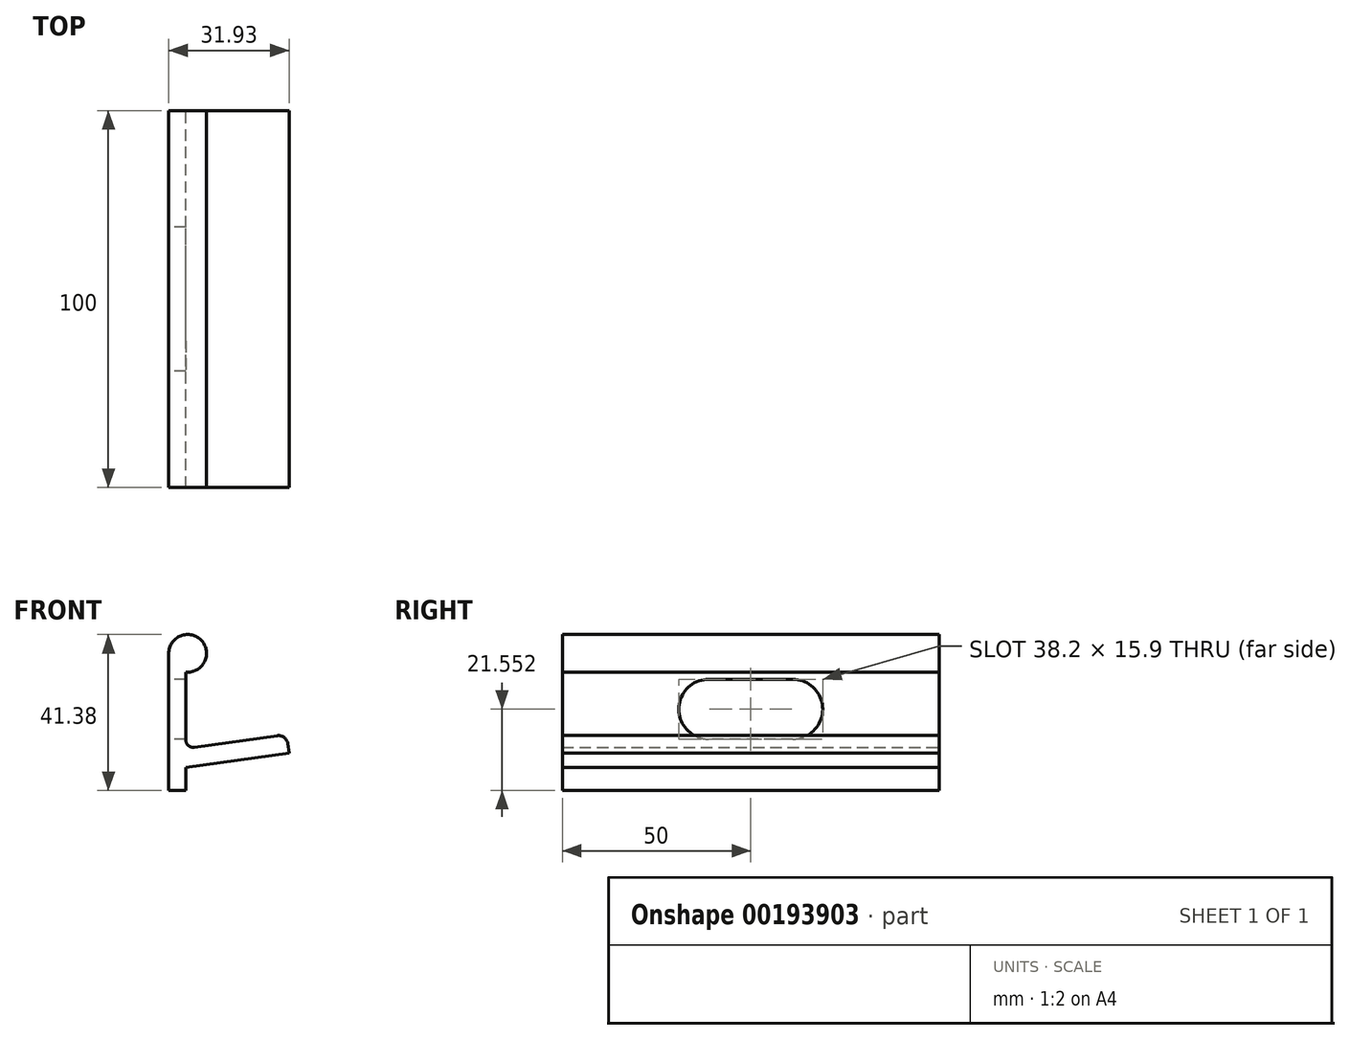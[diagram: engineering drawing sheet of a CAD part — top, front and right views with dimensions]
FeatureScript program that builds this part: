
annotation { "Feature Type Name" : "Feature", "Feature Type Description" : "" }
export const myFeature = defineFeature(function(context is Context, id is Id, definition is map)
    precondition{}
    {
        {
            var Q0;
            Q0=qCreatedBy(makeId("Front.planeOp"),FACE);
            var sketch = newSketch(context, id + "F0", { "sketchPlane" : qUnion([Q0])});
            skLineSegment(sketch, "E0", {"start": v(0, 29.9) * mm, "end": v(0, 7.11) * mm});
            skLineSegment(sketch, "E1", {"start": v(4.5, 23.01) * mm, "end": v(4.5, 7.11) * mm});
            skLineSegment(sketch, "E2", {"start": v(4.5, -0.4) * mm, "end": v(4.5, -6.49) * mm});
            skLineSegment(sketch, "E3", {"start": v(28.76, 8.06) * mm, "end": v(6.78, 4.97) * mm});
            skLineSegment(sketch, "E4", {"start": v(31.59, 5.93) * mm, "end": v(31.93, 3.46) * mm});
            skLineSegment(sketch, "E5", {"start": v(31.93, 3.46) * mm, "end": v(4.5, -0.4) * mm});
            skPoint(sketch, "E6.visualSharp", {"position": v(31.24, 8.4) * mm});
            skArc(sketch, "E6.filletArc", {"start": v(31.59, 5.93) * mm, "mid": v(30.61, 7.58) * mm, "end": v(28.76, 8.06) * mm});
            skLineSegment(sketch, "E7", {"start": v(4.5, 7.11) * mm, "end": v(0, 7.11) * mm});
            skLineSegment(sketch, "E8", {"start": v(4.5, 7.11) * mm, "end": v(4.5, 6.95) * mm});
            skPoint(sketch, "E9.visualSharp", {"position": v(4.5, 4.65) * mm});
            skArc(sketch, "E9.filletArc", {"start": v(4.5, 6.95) * mm, "mid": v(5.19, 5.44) * mm, "end": v(6.78, 4.97) * mm});
            skLineSegment(sketch, "E10", {"start": v(4.5, 23.01) * mm, "end": v(4.5, 24.92) * mm});
            skLineSegment(sketch, "E11", {"start": v(0, 29.9) * mm, "end": v(5, 29.9) * mm, "construction": true});
            skArc(sketch, "E12", {"start": v(4.5, 24.92) * mm, "mid": v(8.7, 33.25) * mm, "end": v(0, 29.9) * mm});
            skLineSegment(sketch, "E13", {"start": v(0, 7.11) * mm, "end": v(0, -6.49) * mm});
            skLineSegment(sketch, "E14", {"start": v(0, -6.49) * mm, "end": v(4.5, -6.49) * mm});
            skLineSegment(sketch, "E15", {"start": v(4.5, 23.01) * mm, "end": v(10.72, 23.01) * mm, "construction": true});
            skLineSegment(sketch, "E16", {"start": v(5, 29.9) * mm, "end": v(5, 34.9) * mm, "construction": true});
            skLineSegment(sketch, "E17", {"start": v(5, 34.9) * mm, "end": v(-15.33, 34.9) * mm, "construction": true});
            skLineSegment(sketch, "E18", {"start": v(-9.2, 4.65) * mm, "end": v(4.5, 4.65) * mm, "construction": true});
            skLineSegment(sketch, "E19", {"start": v(0, 7.11) * mm, "end": v(-9.32, 7.11) * mm, "construction": true});
            skLineSegment(sketch, "E20", {"start": v(4.5, 23.01) * mm, "end": v(0, 23.01) * mm});
            skLineSegment(sketch, "E21", {"start": v(4.5, 11.64) * mm, "end": v(4.5, 6.95) * mm});
            skLineSegment(sketch, "E22", {"start": v(6.78, 4.97) * mm, "end": v(4.5, 4.65) * mm, "construction": true});
            skLineSegment(sketch, "E23", {"start": v(4.5, 4.65) * mm, "end": v(4.5, 7.11) * mm, "construction": true});
            skLineSegment(sketch, "E24", {"start": v(-18.19, 15.06) * mm, "end": v(19.73, 15.06) * mm, "construction": true});
            skSolve(sketch);
        }
        {
            var Q0;
            Q0=makeQuery(id+"F0.imprint","IMPRINT",FACE,{"disambiguationData":[TD([[makeQuery(id+"F0.imprint","IMPRINT",EDGE,{"derivedFrom":sQuery(id+"F0.wireOp",EDGE,"E2")}),-1.0]])]});
            var Q1;
            {var subQ3=sQuery(id+"F0.wireOp",EDGE,"E1");Q1=makeQuery(id+"F0.imprint","IMPRINT",FACE,{"disambiguationData":[TD([[makeQuery(id+"F0.imprint","IMPRINT",EDGE,{"derivedFrom":subQ3}),-1.0]])]});}
            var Q2;
            Q2=makeQuery(id+"F0.imprint","IMPRINT",FACE,{"disambiguationData":[TD([[makeQuery(id+"F0.imprint","IMPRINT",EDGE,{"derivedFrom":sQuery(id+"F0.wireOp",EDGE,"E10")}),1.0]])]});
            extrude(context, id + "F1", {"entities" : qUnion([Q0, Q1, Q2]), "endBound" : BoundingType.SYMMETRIC, "depth" : 100 * mm});
        }
        {
            var Q0;
            Q0=makeQuery(id+"F1.opExtrude","SWEPT_FACE",FACE,{"disambiguationData":[OSD([sQuery(id+"F0.wireOp",EDGE,"E0"),sQuery(id+"F0.wireOp",EDGE,"E13")])]});
            var sketch = newSketch(context, id + "F2", { "sketchPlane" : qUnion([Q0])});
            skLineSegment(sketch, "E25", {"start": v(0, 15.06) * mm, "end": v(19.1, 15.06) * mm, "construction": true});
            skLineSegment(sketch, "E26.MirrorCS", {"start": v(0, 15.06) * mm, "end": v(-19.1, 15.06) * mm, "construction": true});
            skArc(sketch, "E27", {"start": v(11.15, 7.11) * mm, "mid": v(19.1, 15.06) * mm, "end": v(11.15, 23.01) * mm});
            skArc(sketch, "E28", {"start": v(-11.15, 23.01) * mm, "mid": v(-19.1, 15.06) * mm, "end": v(-11.15, 7.11) * mm});
            skLineSegment(sketch, "E29", {"start": v(-11.15, 23.01) * mm, "end": v(11.15, 23.01) * mm});
            skLineSegment(sketch, "E30", {"start": v(11.15, 7.11) * mm, "end": v(-11.15, 7.11) * mm});
            skSolve(sketch);
        }
        {
            var Q0;
            Q0=makeQuery(id+"F2.imprint","IMPRINT",FACE,{"disambiguationData":[TD([[makeQuery(id+"F2.imprint","IMPRINT",EDGE,{"derivedFrom":sQuery(id+"F2.wireOp",EDGE,"E27")}),1.0]])]});
            extrude(context, id + "F3", {"entities" : qUnion([Q0]), "operationType" : NewBodyOperationType.REMOVE, "oppositeDirection" : true, "depth" : 5 * mm});
        }
    });
